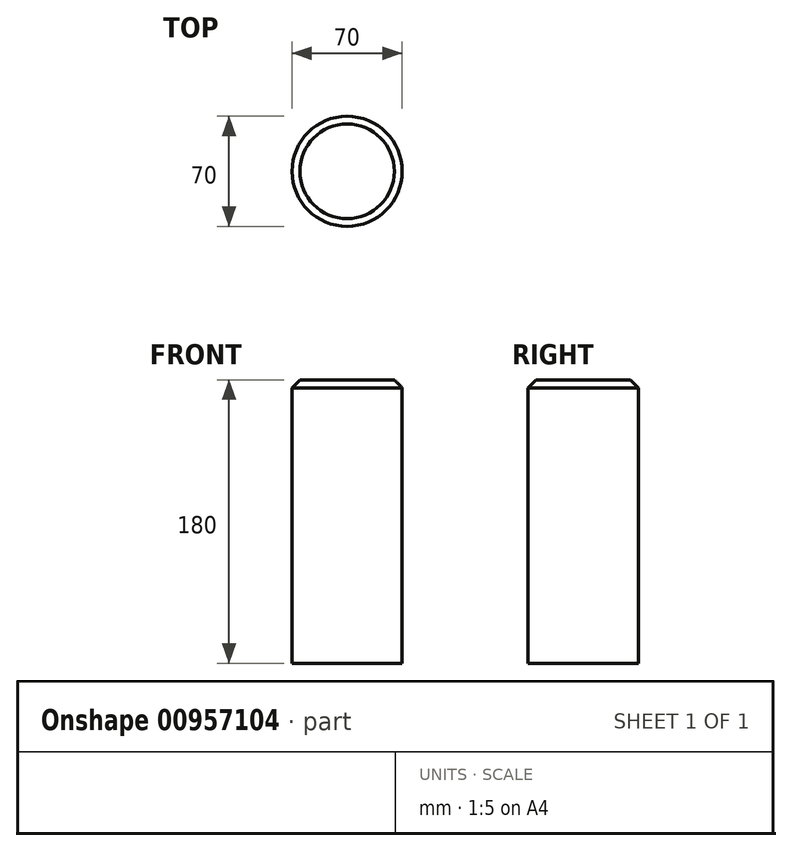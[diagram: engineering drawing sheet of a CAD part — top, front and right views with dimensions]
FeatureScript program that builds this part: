
annotation { "Feature Type Name" : "Feature", "Feature Type Description" : "" }
export const myFeature = defineFeature(function(context is Context, id is Id, definition is map)
    precondition{}
    {
        {
            var Q0;
            Q0=qCreatedBy(makeId("Top.planeOp"),FACE);
            var sketch = newSketch(context, id + "F0", { "sketchPlane" : qUnion([Q0])});
            skCircle(sketch, "E0", {"center": v(0, 0) * mm, "radius": 35 * mm});
            skSolve(sketch);
        }
        {
            var Q0;
            Q0 = qSketchRegion(id + "F0", true);
            extrude(context, id + "F1", {"entities" : qUnion([Q0]), "depth" : 180 * mm, "offsetDistance" : 25 * mm});
        }
        {
            var Q0;
            Q0=makeQuery(id+"F1.opExtrude","CAP_FACE",FACE,{"disambiguationData":[OSD([sQuery(id+"F0.wireOp",EDGE,"E0")])],"isStart":false});
            var Q1;
            Q1=makeQuery(id+"F1.opExtrude","CAP_EDGE",EDGE,{"disambiguationData":[OSD([sQuery(id+"F0.wireOp",EDGE,"E0")])],"isStart":false});
            chamfer(context, id + "F2", {"entities" : qUnion([Q0, Q1]), "width" : 5 * mm, "tangentPropagation" : true});
        }
    });
